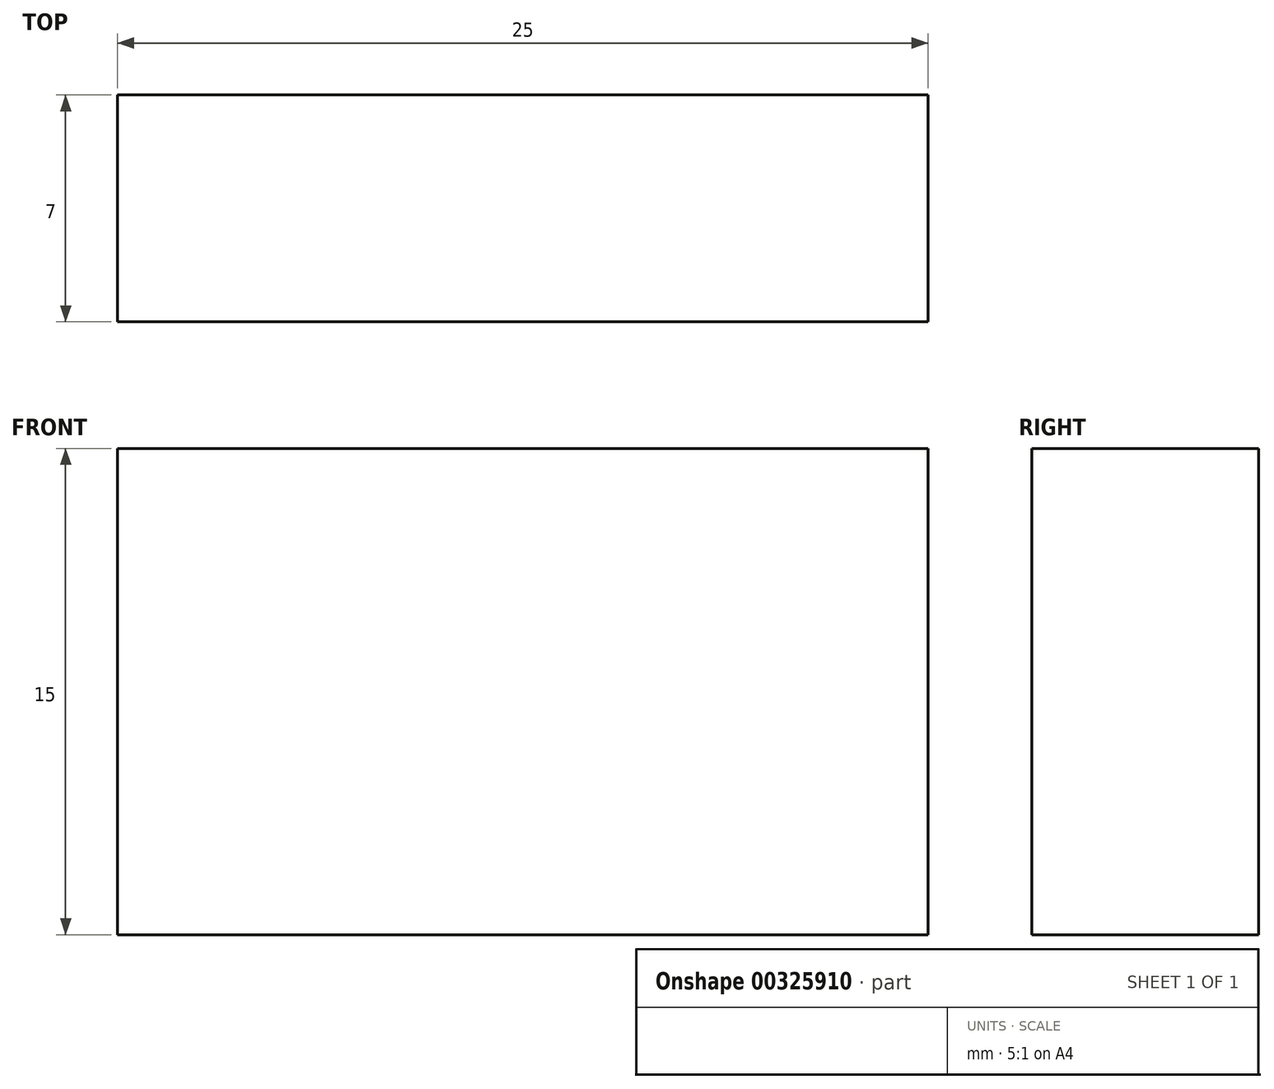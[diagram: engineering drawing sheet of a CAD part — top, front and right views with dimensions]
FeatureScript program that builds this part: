
annotation { "Feature Type Name" : "Feature", "Feature Type Description" : "" }
export const myFeature = defineFeature(function(context is Context, id is Id, definition is map)
    precondition{}
    {
        {
            var Q0;
            Q0=qCreatedBy(makeId("Top.planeOp"),FACE);
            var sketch = newSketch(context, id + "F0", { "sketchPlane" : qUnion([Q0])});
            skLineSegment(sketch, "E0.bottom", {"start": v(12.5, -3.5) * mm, "end": v(-12.5, -3.5) * mm});
            skLineSegment(sketch, "E0.top", {"start": v(12.5, 3.5) * mm, "end": v(-12.5, 3.5) * mm});
            skLineSegment(sketch, "E0.left", {"start": v(12.5, -3.5) * mm, "end": v(12.5, 3.5) * mm});
            skLineSegment(sketch, "E0.right", {"start": v(-12.5, -3.5) * mm, "end": v(-12.5, 3.5) * mm});
            skPoint(sketch, "E0.middle", {"position": v(0, 0) * mm});
            skSolve(sketch);
        }
        {
            var Q0;
            Q0=makeQuery(id+"F0.imprint","IMPRINT",FACE,{"disambiguationData":[TD([[makeQuery(id+"F0.imprint","IMPRINT",EDGE,{"derivedFrom":sQuery(id+"F0.wireOp",EDGE,"E0.bottom")}),-1.0]])]});
            extrude(context, id + "F1", {"entities" : qUnion([Q0]), "depth" : 15 * mm});
        }
    });
